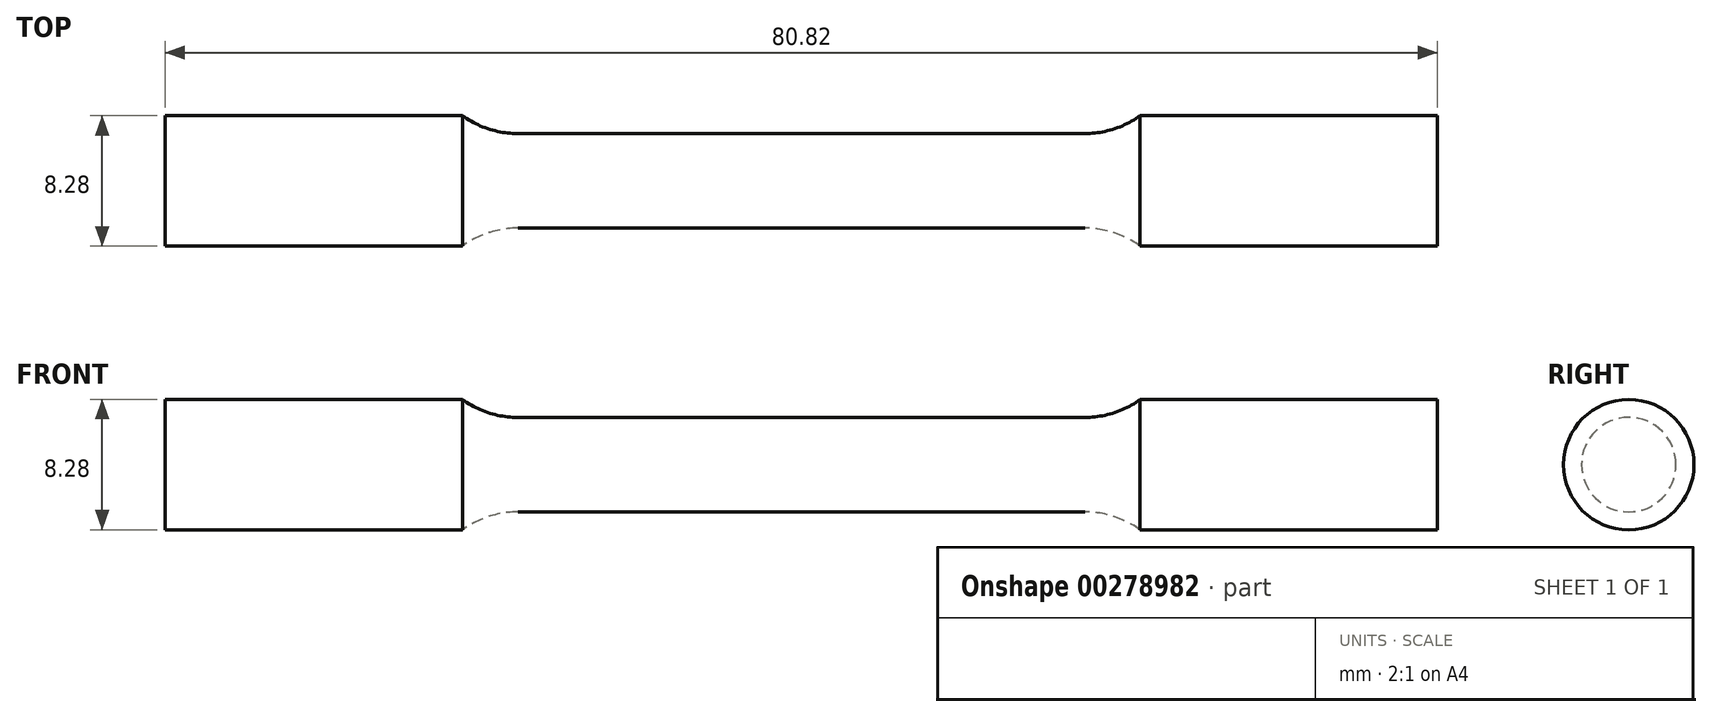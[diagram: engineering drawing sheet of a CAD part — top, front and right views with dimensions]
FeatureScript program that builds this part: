
annotation { "Feature Type Name" : "Feature", "Feature Type Description" : "" }
export const myFeature = defineFeature(function(context is Context, id is Id, definition is map)
    precondition{}
    {
        {
            var Q0;
            Q0=qCreatedBy(makeId("Front.planeOp"),FACE);
            var sketch = newSketch(context, id + "F0", { "sketchPlane" : qUnion([Q0])});
            skLineSegment(sketch, "E0", {"start": v(0, 3) * mm, "end": v(18, 3) * mm});
            skArc(sketch, "E1", {"start": v(18, 3) * mm, "mid": v(19.85, 3.3) * mm, "end": v(21.52, 4.14) * mm});
            skLineSegment(sketch, "E2", {"start": v(21.52, 4.14) * mm, "end": v(40.4, 4.14) * mm});
            skLineSegment(sketch, "E3", {"start": v(40.4, 4.14) * mm, "end": v(40.4, 0) * mm});
            skLineSegment(sketch, "E4.MirrorCS", {"start": v(-21.52, 4.14) * mm, "end": v(-40.4, 4.14) * mm});
            skLineSegment(sketch, "E5.MirrorCS", {"start": v(-40.4, 4.14) * mm, "end": v(-40.4, 0) * mm});
            skLineSegment(sketch, "E6.MirrorCS", {"start": v(0, 3) * mm, "end": v(-18, 3) * mm});
            skArc(sketch, "E7.MirrorCS", {"start": v(-18, 3) * mm, "mid": v(-19.85, 3.3) * mm, "end": v(-21.52, 4.14) * mm});
            skLineSegment(sketch, "E8", {"start": v(-40.4, 0) * mm, "end": v(40.4, 0) * mm});
            skSolve(sketch);
        }
        {
            var Q0;
            Q0=makeQuery(id+"F0.imprint","IMPRINT",FACE,{"disambiguationData":[TD([[makeQuery(id+"F0.imprint","IMPRINT",EDGE,{"derivedFrom":sQuery(id+"F0.wireOp",EDGE,"E0")}),-1.0]])]});
            var Q1;
            Q1=sQuery(id+"F0.wireOp",EDGE,"E8");
            revolve(context, id + "F1", {"entities" : qUnion([Q0]), "axis" : qUnion([Q1]), "revolveType" : RevolveType.FULL});
        }
    });
